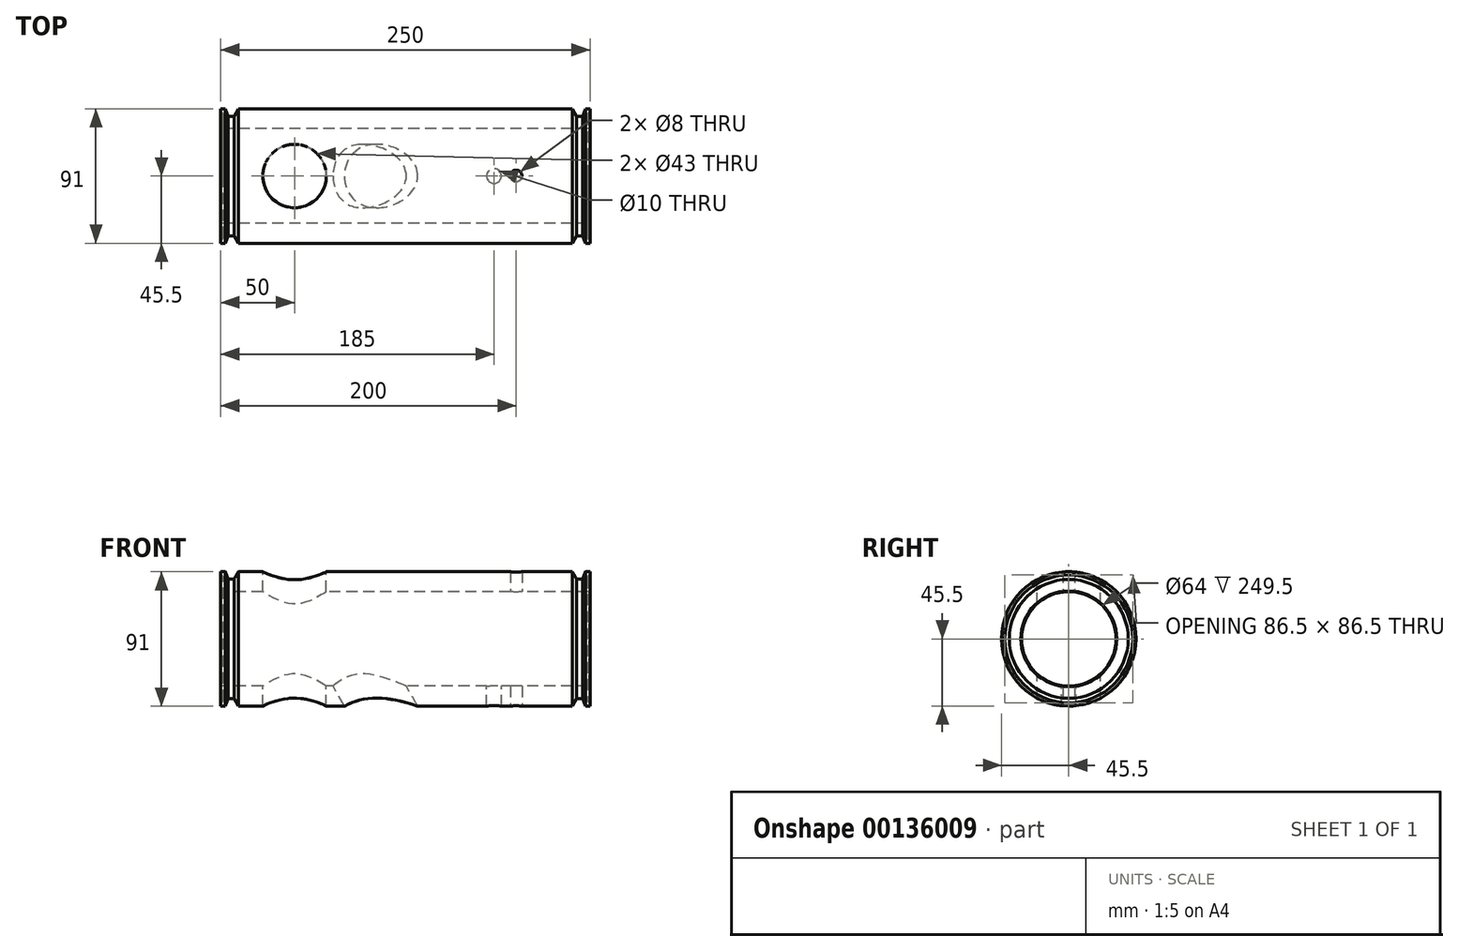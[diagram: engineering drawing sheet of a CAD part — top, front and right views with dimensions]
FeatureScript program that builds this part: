
annotation { "Feature Type Name" : "Feature", "Feature Type Description" : "" }
export const myFeature = defineFeature(function(context is Context, id is Id, definition is map)
    precondition{}
    {
        {
            var Q0;
            Q0=qCreatedBy(makeId("Right.planeOp"),FACE);
            var sketch = newSketch(context, id + "F0", { "sketchPlane" : qUnion([Q0])});
            skCircle(sketch, "E0", {"center": v(0, 0) * mm, "radius": 32 * mm});
            skCircle(sketch, "E1", {"center": v(0, 0) * mm, "radius": 45.5 * mm});
            skSolve(sketch);
        }
        {
            var Q0;
            Q0=qSketchRegion(id+"F0",true);
            extrude(context, id + "F1", {"entities" : qUnion([Q0]), "depth" : 200 * mm});
        }
        {
            var Q0;
            Q0=qCreatedBy(makeId("Right.planeOp"),FACE);
            cPlane(context, id + "F2", {"entities" : qUnion([Q0]), "cplaneType" : CPlaneType.OFFSET, "offset" : 200 * mm, "width" : 150 * mm, "height" : 150 * mm});
        }
        {
            var Q0;
            Q0=qCreatedBy(makeId("Right.planeOp"),FACE);
            var sketch = newSketch(context, id + "F3", { "sketchPlane" : qUnion([Q0])});
            skCircle(sketch, "E2", {"center": v(0, 0) * mm, "radius": 32 * mm});
            skCircle(sketch, "E3", {"center": v(0, 0) * mm, "radius": 45.5 * mm});
            skSolve(sketch);
        }
        {
            var Q0;
            Q0=qSketchRegion(id+"F3",true);
            extrude(context, id + "F4", {"entities" : qUnion([Q0]), "operationType" : NewBodyOperationType.ADD, "oppositeDirection" : true, "depth" : 50 * mm});
        }
        {
            var Q0;
            Q0=qCreatedBy(makeId("Front.planeOp"),FACE);
            var sketch = newSketch(context, id + "F5", { "sketchPlane" : qUnion([Q0])});
            skLineSegment(sketch, "E4", {"start": v(0, 0) * mm, "end": v(200, 0) * mm, "construction": true});
            skLineSegment(sketch, "E5", {"start": v(200, 0) * mm, "end": v(200, 45.5) * mm, "construction": true});
            skLineSegment(sketch, "E6", {"start": v(200, 45.5) * mm, "end": v(196.8, 45.5) * mm, "construction": true});
            skLineSegment(sketch, "E7", {"start": v(196.8, 45.5) * mm, "end": v(194.97, 40.48) * mm});
            skLineSegment(sketch, "E8", {"start": v(194.97, 40.48) * mm, "end": v(190.97, 40.48) * mm});
            skLineSegment(sketch, "E9", {"start": v(190.97, 40.48) * mm, "end": v(188.08, 45.5) * mm});
            skLineSegment(sketch, "E10", {"start": v(188.08, 45.5) * mm, "end": v(196.8, 45.5) * mm});
            skLineSegment(sketch, "E11", {"start": v(200, 0) * mm, "end": v(-50, 0) * mm, "construction": true});
            skLineSegment(sketch, "E12", {"start": v(75, 0) * mm, "end": v(75, 86.7) * mm, "construction": true});
            skPoint(sketch, "E12.endSnap0", {"position": v(75, 0) * mm});
            skLineSegment(sketch, "E13.MirrorCS", {"start": v(-40.97, 40.48) * mm, "end": v(-38.08, 45.5) * mm});
            skLineSegment(sketch, "E14.MirrorCS", {"start": v(-38.08, 45.5) * mm, "end": v(-46.8, 45.5) * mm});
            skLineSegment(sketch, "E15.MirrorCS", {"start": v(-44.97, 40.48) * mm, "end": v(-40.97, 40.48) * mm});
            skLineSegment(sketch, "E16.MirrorCS", {"start": v(-46.8, 45.5) * mm, "end": v(-44.97, 40.48) * mm});
            skCircle(sketch, "E17", {"center": v(200, 41.75) * mm, "radius": 1.5 * mm});
            skCircle(sketch, "E18", {"center": v(-50.02, 41.75) * mm, "radius": 1.5 * mm});
            skSolve(sketch);
        }
        {
            var Q0;
            Q0=qSketchRegion(id+"F5",true);
            var Q1;
            Q1=sQuery(id+"F5.wireOp",EDGE,"E4");
            revolve(context, id + "F6", {"operationType" : NewBodyOperationType.REMOVE, "entities" : qUnion([Q0]), "axis" : qUnion([Q1]), "revolveType" : RevolveType.FULL});
        }
        {
            var Q0;
            Q0=qCreatedBy(makeId("Top.planeOp"),FACE);
            var sketch = newSketch(context, id + "F7", { "sketchPlane" : qUnion([Q0])});
            skCircle(sketch, "E19", {"center": v(135, 0) * mm, "radius": 5 * mm});
            skSolve(sketch);
        }
        {
            var Q0;
            Q0=qSketchRegion(id+"F7",true);
            extrude(context, id + "F8", {"entities" : qUnion([Q0]), "operationType" : NewBodyOperationType.REMOVE, "oppositeDirection" : true, "depth" : 51.26 * mm});
        }
        {
            var Q0;
            Q0=qCreatedBy(makeId("Top.planeOp"),FACE);
            cPlane(context, id + "F9", {"entities" : qUnion([Q0]), "cplaneType" : CPlaneType.OFFSET, "offset" : 45.5 * mm, "oppositeDirection" : true, "width" : 150 * mm, "height" : 150 * mm});
        }
        {
            var Q0;
            Q0=qCreatedBy(id+"F9.planeOp",FACE);
            var sketch = newSketch(context, id + "F10", { "sketchPlane" : qUnion([Q0])});
            skCircle(sketch, "E20", {"center": v(150, 0) * mm, "radius": 4 * mm});
            skSolve(sketch);
        }
        {
            var Q0;
            Q0=qSketchRegion(id+"F10",true);
            extrude(context, id + "F11", {"entities" : qUnion([Q0]), "operationType" : NewBodyOperationType.REMOVE, "endBound" : BoundingType.THROUGH_ALL, "depth" : 25 * mm});
        }
        {
            var Q0;
            Q0=makeQuery(id+"F1.opExtrude","CAP_EDGE",EDGE,{"disambiguationData":[OSD([sQuery(id+"F0.wireOp",EDGE,"E0")])],"isStart":false});
            chamfer(context, id + "F12", {"entities" : qUnion([Q0]), "width" : 0.5 * mm, "tangentPropagation" : true});
        }
        {
            var Q0;
            Q0=qCreatedBy(makeId("Top.planeOp"),FACE);
            var sketch = newSketch(context, id + "F13", { "sketchPlane" : qUnion([Q0])});
            skCircle(sketch, "E21", {"center": v(0, 0) * mm, "radius": 21.5 * mm});
            skSolve(sketch);
        }
        {
            var Q0;
            Q0 = qSketchRegion(id + "F13", true);
            extrude(context, id + "F14", {"entities" : qUnion([Q0]), "operationType" : NewBodyOperationType.REMOVE, "endBound" : BoundingType.SYMMETRIC, "oppositeDirection" : true, "depth" : 100 * mm});
        }
        {
            var Q0;
            Q0=qCreatedBy(makeId("Top.planeOp"),FACE);
            var sketch = newSketch(context, id + "F15", { "sketchPlane" : qUnion([Q0])});
            skPoint(sketch, "E22.0", {"position": v(0, 0) * mm});
            skLineSegment(sketch, "E23", {"start": v(0, 0) * mm, "end": v(0, 56.28) * mm, "construction": true});
            skSolve(sketch);
        }
        {
            var Q0;
            Q0=qCreatedBy(makeId("Top.planeOp"),FACE);
            var Q1;
            Q1=sQuery(id+"F15.wireOp",EDGE,"E23");
            cPlane(context, id + "F16", {"entities" : qUnion([Q0, Q1]), "cplaneType" : CPlaneType.LINE_ANGLE, "offset" : 25 * mm, "angle" : 150 * degree, "width" : 150 * mm, "height" : 150 * mm});
        }
        {
            var Q0;
            Q0=qCreatedBy(id+"F16.planeOp",FACE);
            cPlane(context, id + "F17", {"entities" : qUnion([Q0]), "cplaneType" : CPlaneType.OFFSET, "offset" : 30 * mm, "oppositeDirection" : true, "width" : 150 * mm, "height" : 150 * mm});
        }
        {
            var Q0;
            Q0=qCreatedBy(makeId("Top.planeOp"),FACE);
            var sketch = newSketch(context, id + "F18", { "sketchPlane" : qUnion([Q0])});
            skPoint(sketch, "E24.0", {"position": v(0, 0) * mm});
            skLineSegment(sketch, "E25", {"start": v(0, 0) * mm, "end": v(84.57, 0) * mm, "construction": true});
            skSolve(sketch);
        }
        {
            var Q0;
            Q0=qCreatedBy(id+"F17.planeOp",FACE);
            var sketch = newSketch(context, id + "F19", { "sketchPlane" : qUnion([Q0])});
            skPoint(sketch, "E26.0", {"position": v(0, 0) * mm});
            skLineSegment(sketch, "E27", {"start": v(0, 0) * mm, "end": v(117.8, 0) * mm, "construction": true});
            skCircle(sketch, "E28", {"center": v(28, 0) * mm, "radius": 21.5 * mm});
            skSolve(sketch);
        }
        {
            var Q0;
            Q0 = qSketchRegion(id + "F19", true);
            extrude(context, id + "F20", {"entities" : qUnion([Q0]), "operationType" : NewBodyOperationType.REMOVE, "oppositeDirection" : true, "depth" : 67 * mm});
        }
    });
